# Revit family: Valve-Six_Outlet_HP-KOHLER-K-28212_1
name_source: partatom
category: Plumbing Fixtures
revit_build: Autodesk Revit 2017 (Build: 20160225_1515(x64)
units: mm (PartAtom-declared; Revit-internal decimal feet)

## family parameters
Cut with Voids When Loaded = No
Host = Face
OmniClass Number = 23.27.31.00
OmniClass Title = Valves
Part Type = Normal
Room Calculation Point = No
Round Connector Dimension = Use Diameter
Shared = No

## types (1)
- NA-Not Applicable
    ADA Compliant = No
    Apparent Load = 60 VA
    Assembly Code = D2020
    CW Connection = Yes
    Cold Water Inlet = Cold Water Inlet
    Date Modified = 02/11/2021
    Default Elevation = 0"
    Description = 6 OUTLET HP VALVE US
    Electrical Connector = Yes
    Electrical Note = One dedicated circuit required
    Finish = Kohler-Plastic-7-Black_Black
    Flow Rate = 26 GPM
    HW Connection = Yes
    Height = 3"
    Hot Water Inlet = Hot Water Inlet
    Length = 10 11/16"
    Manufacturer = KOHLER Co.
    Master Format 2014 = 23 09 13.33
    Master Format 2014 Name = Control Valves
    Material = Brass Construction
    Model = K-28212-NA
    Pressure = 72.50 psi
    Product Documentation Link = https://www.us.kohler.com
    Product Page URL = http://www.us.kohler.com
    Tempered Water Outlet 1 = Tempered Water Outlet 1
    Tempered Water Outlet 2 = Tempered Water Outlet 2
    Tempered Water Outlet 3 = Tempered Water Outlet 3
    Tempered Water Outlet 4 = Tempered Water Outlet 4
    Tempered Water Outlet 5 = Tempered Water Outlet 5
    Tempered Water Outlet 6 = Tempered Water Outlet 6
    Type = 1
    URL = https://www.us.kohler.com
    Vent Connection = No
    Voltage = 12 V
    Waste Connection = No
    Waste Water Outlet = Waste Water Outlet
    WaterSense Certified = No
    Width = 21 1/8"

## geometry (parser evidence)
native form markers: Sweep x4
no freeform markers — native parametric forms only
